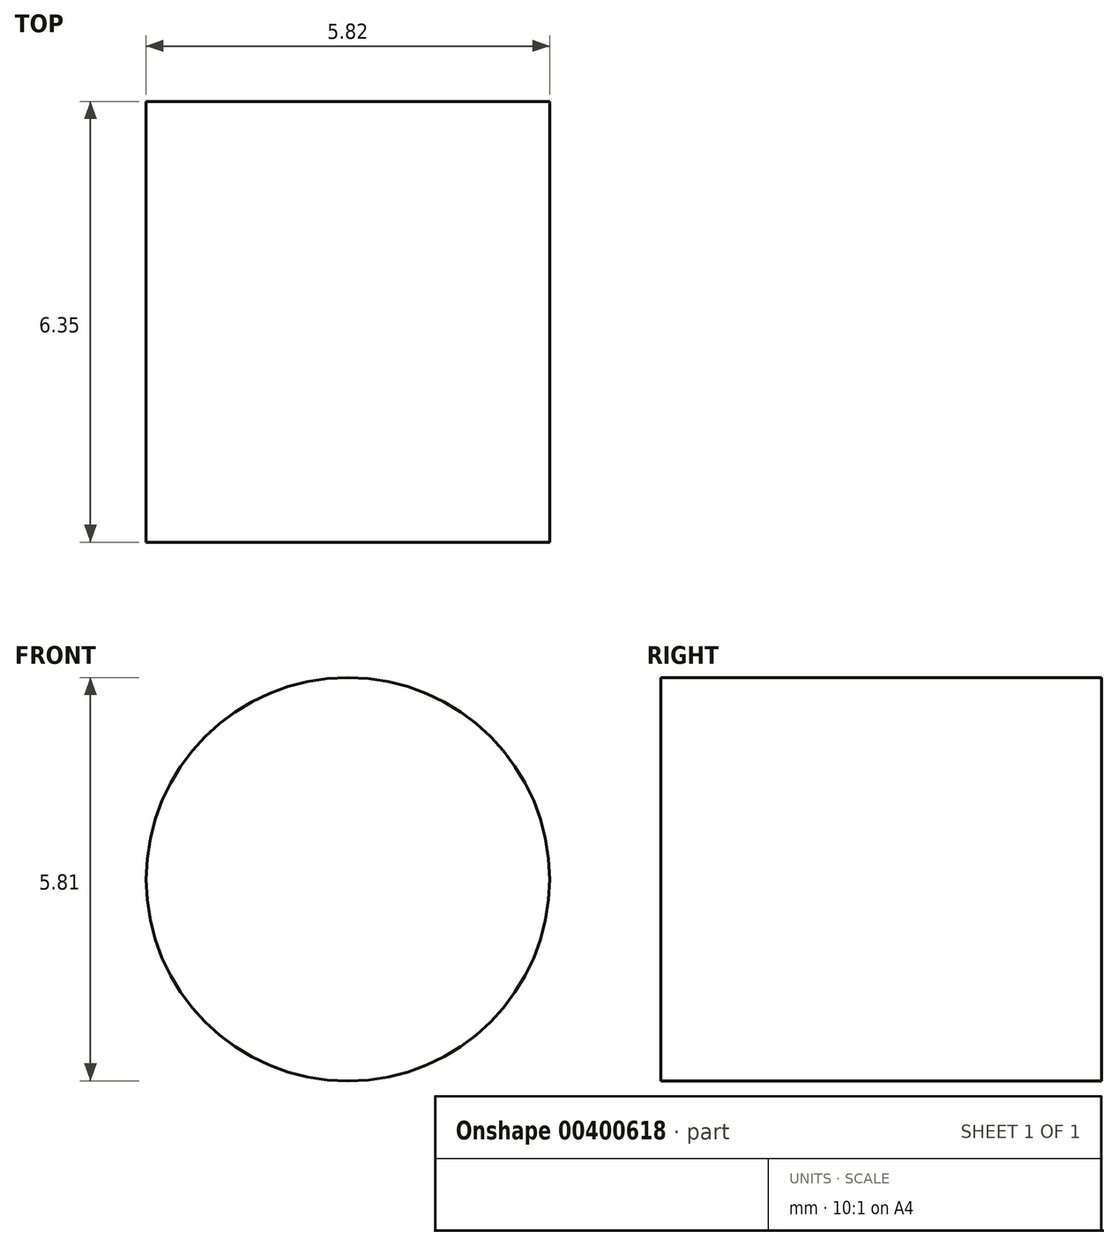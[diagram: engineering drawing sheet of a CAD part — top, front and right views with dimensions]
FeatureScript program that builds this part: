
annotation { "Feature Type Name" : "Feature", "Feature Type Description" : "" }
export const myFeature = defineFeature(function(context is Context, id is Id, definition is map)
    precondition{}
    {
        {
            var Q0;
            Q0=qCreatedBy(makeId("Front.planeOp"),FACE);
            var sketch = newSketch(context, id + "F0", { "sketchPlane" : qUnion([Q0])});
            skCircle(sketch, "E0", {"center": v(-19.86, 2.63) * mm, "radius": 2.9 * mm});
            skSolve(sketch);
        }
        {
            var Q0;
            Q0=makeQuery(id+"F0.imprint","IMPRINT",FACE,{"disambiguationData":[TD([[makeQuery(id+"F0.imprint","IMPRINT",EDGE,{"derivedFrom":sQuery(id+"F0.wireOp",EDGE,"E0")}),1.0]])]});
            extrude(context, id + "F1", {"entities" : qUnion([Q0]), "depth" : 6.35 * mm});
        }
    });
